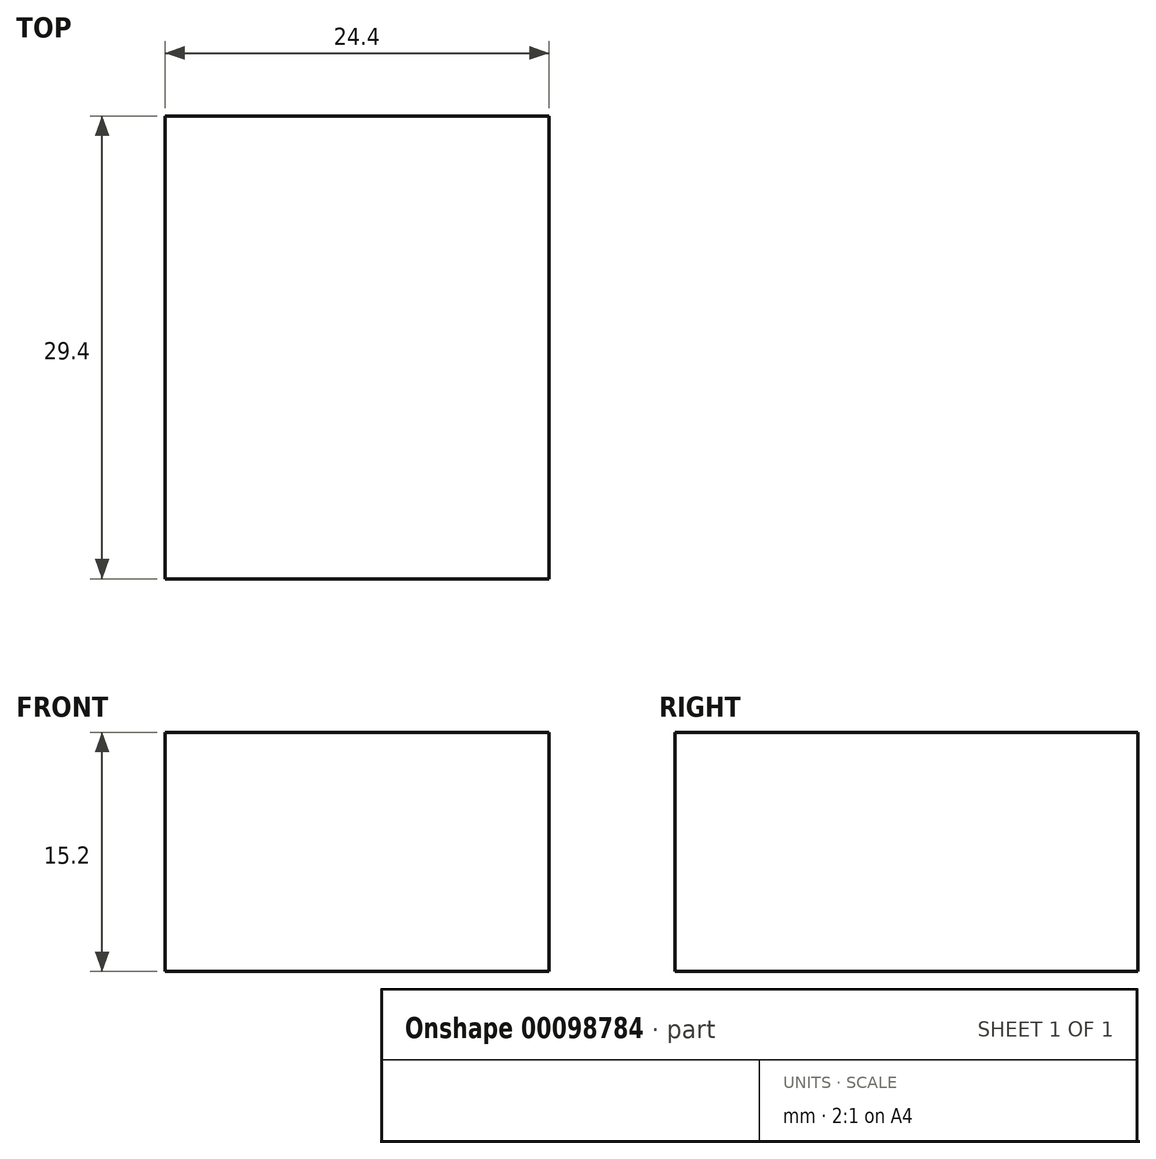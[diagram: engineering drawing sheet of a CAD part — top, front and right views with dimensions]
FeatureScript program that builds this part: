
annotation { "Feature Type Name" : "Feature", "Feature Type Description" : "" }
export const myFeature = defineFeature(function(context is Context, id is Id, definition is map)
    precondition{}
    {
        {
            var Q0;
            Q0=qCreatedBy(makeId("Front.planeOp"),FACE);
            var sketch = newSketch(context, id + "F0", { "sketchPlane" : qUnion([Q0])});
            skLineSegment(sketch, "E0", {"start": v(0, 0) * mm, "end": v(0, 15.2) * mm});
            skLineSegment(sketch, "E1", {"start": v(0, 15.2) * mm, "end": v(24.4, 15.2) * mm});
            skLineSegment(sketch, "E2", {"start": v(24.4, 15.2) * mm, "end": v(24.4, 0) * mm});
            skLineSegment(sketch, "E3", {"start": v(24.4, 0) * mm, "end": v(0, 0) * mm});
            skSolve(sketch);
        }
        {
            var Q0;
            Q0 = qSketchRegion(id + "F0", true);
            extrude(context, id + "F1", {"entities" : qUnion([Q0]), "depth" : 29.4 * mm});
        }
    });
